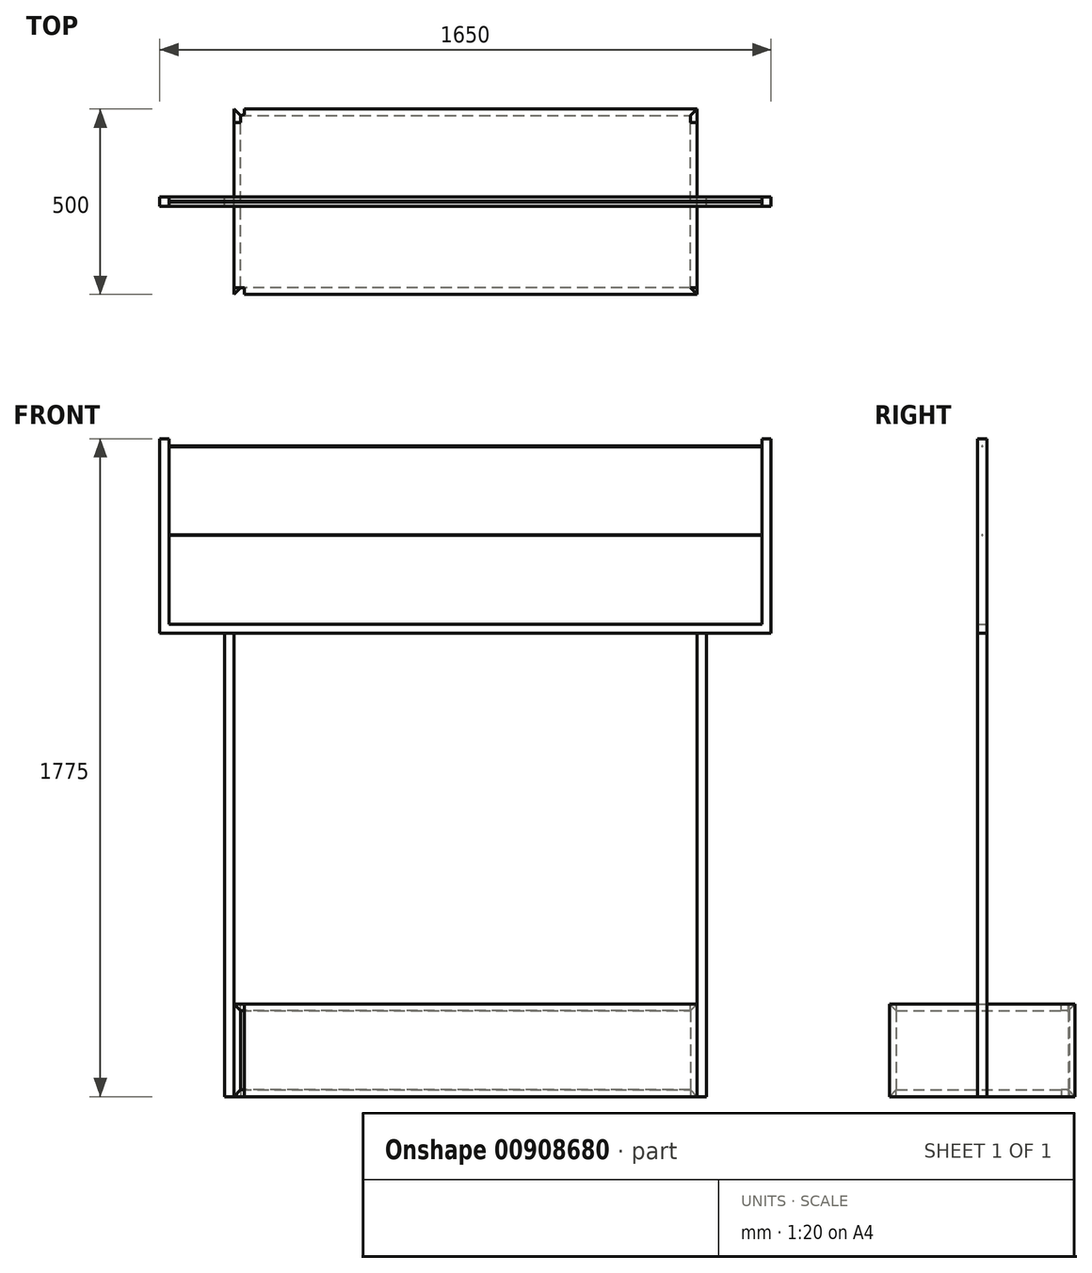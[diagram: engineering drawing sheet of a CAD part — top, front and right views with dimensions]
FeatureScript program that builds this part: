
annotation { "Feature Type Name" : "Feature", "Feature Type Description" : "" }
export const myFeature = defineFeature(function(context is Context, id is Id, definition is map)
    precondition{}
    {
        {
            var Q0;
            Q0=qCreatedBy(makeId("Front.planeOp"),FACE);
            var sketch = newSketch(context, id + "F0", { "sketchPlane" : qUnion([Q0])});
            skLineSegment(sketch, "E0", {"start": v(-625, 0) * mm, "end": v(625, 0) * mm});
            skLineSegment(sketch, "E1", {"start": v(625, 0) * mm, "end": v(607, 18) * mm});
            skLineSegment(sketch, "E2", {"start": v(607, 18) * mm, "end": v(-607, 18) * mm});
            skLineSegment(sketch, "E3", {"start": v(-607, 18) * mm, "end": v(-625, 0) * mm});
            skSolve(sketch);
        }
        {
            var Q0;
            Q0=qSketchRegion(id+"F0",true);
            extrude(context, id + "F1", {"entities" : qUnion([Q0]), "endBound" : BoundingType.SYMMETRIC, "depth" : 500 * mm, "offsetDistance" : 25 * mm});
        }
        {
            var Q0;
            Q0=qCreatedBy(makeId("Right.planeOp"),FACE);
            var sketch = newSketch(context, id + "F2", { "sketchPlane" : qUnion([Q0])});
            skLineSegment(sketch, "E4", {"start": v(-250, 0) * mm, "end": v(-231.1, 18.9) * mm});
            skLineSegment(sketch, "E5", {"start": v(-231.1, 18.9) * mm, "end": v(-231.1, 28.41) * mm});
            skLineSegment(sketch, "E6", {"start": v(-231.1, 28.41) * mm, "end": v(-266.04, 28.41) * mm});
            skLineSegment(sketch, "E7", {"start": v(-266.04, 28.41) * mm, "end": v(-266.04, 0) * mm});
            skLineSegment(sketch, "E8", {"start": v(-266.04, 0) * mm, "end": v(-250, 0) * mm});
            skLineSegment(sketch, "E9", {"start": v(250, 0) * mm, "end": v(231.1, 18.9) * mm});
            skLineSegment(sketch, "E10", {"start": v(231.1, 18.9) * mm, "end": v(231.1, 44) * mm});
            skLineSegment(sketch, "E11", {"start": v(231.1, 44) * mm, "end": v(262.92, 44) * mm});
            skLineSegment(sketch, "E12", {"start": v(262.92, 44) * mm, "end": v(262.92, 0) * mm});
            skLineSegment(sketch, "E13", {"start": v(250, 0) * mm, "end": v(262.92, 0) * mm});
            skSolve(sketch);
        }
        {
            var Q0;
            Q0=qSketchRegion(id+"F2",true);
            extrude(context, id + "F3", {"entities" : qUnion([Q0]), "operationType" : NewBodyOperationType.REMOVE, "endBound" : BoundingType.SYMMETRIC, "oppositeDirection" : true, "depth" : 1428 * mm, "offsetDistance" : 25 * mm});
        }
        {
            var Q0;
            Q0=qCreatedBy(makeId("Right.planeOp"),FACE);
            var sketch = newSketch(context, id + "F4", { "sketchPlane" : qUnion([Q0])});
            skLineSegment(sketch, "E14.0", {"start": v(232, 18) * mm, "end": v(250, 0) * mm});
            skLineSegment(sketch, "E14.1", {"start": v(-232, 18) * mm, "end": v(-250, 0) * mm});
            skLineSegment(sketch, "E15", {"start": v(232, 18) * mm, "end": v(232, 232) * mm});
            skLineSegment(sketch, "E16", {"start": v(232, 232) * mm, "end": v(250, 250) * mm});
            skLineSegment(sketch, "E17", {"start": v(250, 250) * mm, "end": v(250, 0) * mm});
            skLineSegment(sketch, "E18", {"start": v(-232, 18) * mm, "end": v(-232, 232) * mm});
            skLineSegment(sketch, "E19", {"start": v(-232, 232) * mm, "end": v(-250, 250) * mm});
            skLineSegment(sketch, "E20", {"start": v(-250, 250) * mm, "end": v(-250, 0) * mm});
            skSolve(sketch);
        }
        {
            var Q0;
            Q0=makeQuery(id+"F4.imprint","IMPRINT",FACE,{"disambiguationData":[TD([[makeQuery(id+"F4.imprint","IMPRINT",EDGE,{"derivedFrom":sQuery(id+"F4.wireOp",EDGE,"E14.0")}),1.0]])]});
            var Q1;
            Q1=makeQuery(id+"F4.imprint","IMPRINT",FACE,{"disambiguationData":[TD([[makeQuery(id+"F4.imprint","IMPRINT",EDGE,{"derivedFrom":sQuery(id+"F4.wireOp",EDGE,"E14.1")}),-1.0]])]});
            var Q2;
            Q2=makeQuery(id+"F1.opExtrude","CAP_VERTEX",VERTEX,{"disambiguationData":[OSD([sQuery(id+"F0.wireOp",EDGE,"E0"),sQuery(id+"F0.wireOp",EDGE,"E1")])],"isStart":true});
            extrude(context, id + "F5", {"entities" : qUnion([Q0, Q1]), "endBound" : BoundingType.SYMMETRIC, "depth" : 1250 * mm, "endBoundEntityVertex" : qUnion([Q2]), "offsetDistance" : 25 * mm});
        }
        {
            var Q0;
            Q0=qCreatedBy(makeId("Top.planeOp"),FACE);
            var sketch = newSketch(context, id + "F6", { "sketchPlane" : qUnion([Q0])});
            skLineSegment(sketch, "E21", {"start": v(-625, 250) * mm, "end": v(-607, 232) * mm});
            skLineSegment(sketch, "E22", {"start": v(-607, 232) * mm, "end": v(-607, 212.8) * mm});
            skLineSegment(sketch, "E23", {"start": v(-607, 212.8) * mm, "end": v(-625, 212.8) * mm});
            skLineSegment(sketch, "E24", {"start": v(-625, 212.8) * mm, "end": v(-625, 250) * mm});
            skLineSegment(sketch, "E25", {"start": v(-607, -232) * mm, "end": v(-625, -250) * mm});
            skLineSegment(sketch, "E26", {"start": v(-625, -250) * mm, "end": v(-638.85, -250) * mm});
            skLineSegment(sketch, "E27", {"start": v(-638.85, -250) * mm, "end": v(-638.85, -232) * mm});
            skLineSegment(sketch, "E28", {"start": v(-638.85, -232) * mm, "end": v(-607, -232) * mm});
            skLineSegment(sketch, "E29.MirrorCS", {"start": v(625, 250) * mm, "end": v(607, 232) * mm});
            skLineSegment(sketch, "E30.MirrorCS", {"start": v(638.85, -232) * mm, "end": v(607, -232) * mm});
            skLineSegment(sketch, "E31.MirrorCS", {"start": v(638.85, -250) * mm, "end": v(638.85, -232) * mm});
            skLineSegment(sketch, "E32.MirrorCS", {"start": v(607, -232) * mm, "end": v(625, -250) * mm});
            skLineSegment(sketch, "E33.MirrorCS", {"start": v(607, 232) * mm, "end": v(607, 212.8) * mm});
            skLineSegment(sketch, "E34.MirrorCS", {"start": v(625, -250) * mm, "end": v(638.85, -250) * mm});
            skLineSegment(sketch, "E35.MirrorCS", {"start": v(607, 212.8) * mm, "end": v(625, 212.8) * mm});
            skLineSegment(sketch, "E36.MirrorCS", {"start": v(625, 212.8) * mm, "end": v(625, 250) * mm});
            skSolve(sketch);
        }
        {
            var Q0;
            Q0=qSketchRegion(id+"F6",true);
            extrude(context, id + "F7", {"entities" : qUnion([Q0]), "operationType" : NewBodyOperationType.REMOVE, "endBound" : BoundingType.SYMMETRIC, "depth" : 1216 * mm, "offsetDistance" : 25 * mm});
        }
        {
            var Q0;
            Q0=qCreatedBy(makeId("Front.planeOp"),FACE);
            var sketch = newSketch(context, id + "F8", { "sketchPlane" : qUnion([Q0])});
            skLineSegment(sketch, "E37.0", {"start": v(-625, 0) * mm, "end": v(-607, 18) * mm});
            skLineSegment(sketch, "E37.1", {"start": v(-607, 232) * mm, "end": v(-607, 18) * mm});
            skLineSegment(sketch, "E37.2", {"start": v(-625, 250) * mm, "end": v(-625, 0) * mm});
            skLineSegment(sketch, "E37.3", {"start": v(-607, 232) * mm, "end": v(-625, 250) * mm});
            skSolve(sketch);
        }
        {
            var Q0;
            Q0=qSketchRegion(id+"F8",true);
            extrude(context, id + "F9", {"entities" : qUnion([Q0]), "endBound" : BoundingType.SYMMETRIC, "depth" : 500 * mm, "offsetDistance" : 25 * mm});
        }
        {
            var Q0;
            Q0=qCreatedBy(makeId("Top.planeOp"),FACE);
            var sketch = newSketch(context, id + "F10", { "sketchPlane" : qUnion([Q0])});
            skLineSegment(sketch, "E38.0", {"start": v(-607, -232) * mm, "end": v(-625, -250) * mm});
            skLineSegment(sketch, "E38.1", {"start": v(-607, 232) * mm, "end": v(-625, 250) * mm});
            skLineSegment(sketch, "E39", {"start": v(-625, 250) * mm, "end": v(-625, 288.49) * mm});
            skLineSegment(sketch, "E40", {"start": v(-625, 288.49) * mm, "end": v(-596.8, 288.49) * mm});
            skLineSegment(sketch, "E41", {"start": v(-596.8, 288.49) * mm, "end": v(-596.8, 234.6) * mm});
            skLineSegment(sketch, "E42", {"start": v(-596.8, 234.6) * mm, "end": v(-607, 232) * mm});
            skLineSegment(sketch, "E43", {"start": v(-607, -232) * mm, "end": v(-596.8, -232) * mm});
            skLineSegment(sketch, "E44", {"start": v(-596.8, -232) * mm, "end": v(-596.8, -280.72) * mm});
            skLineSegment(sketch, "E45", {"start": v(-596.8, -280.72) * mm, "end": v(-625, -280.72) * mm});
            skLineSegment(sketch, "E46", {"start": v(-625, -280.72) * mm, "end": v(-625, -250) * mm});
            skSolve(sketch);
        }
        {
            var Q0;
            Q0=qSketchRegion(id+"F10",true);
            extrude(context, id + "F11", {"entities" : qUnion([Q0]), "operationType" : NewBodyOperationType.REMOVE, "endBound" : BoundingType.SYMMETRIC, "depth" : 1068 * mm, "offsetDistance" : 25 * mm});
        }
        {
            var Q0;
            Q0=makeQuery(id+"F9.opExtrude","SWEPT_BODY",BODY,{"disambiguationData":[OSD([sQuery(id+"F8.wireOp",EDGE,"E37.0"),sQuery(id+"F8.wireOp",EDGE,"E37.1"),sQuery(id+"F8.wireOp",EDGE,"E37.2"),sQuery(id+"F8.wireOp",EDGE,"E37.3")])]});
            var Q1;
            Q1=qCreatedBy(makeId("Right.planeOp"),FACE);
            mirror(context, id + "F12", {"entities" : qUnion([Q0]), "mirrorPlane" : qUnion([Q1])});
        }
        {
            var Q0;
            Q0=qCreatedBy(makeId("Top.planeOp"),FACE);
            cPlane(context, id + "F13", {"entities" : qUnion([Q0]), "cplaneType" : CPlaneType.OFFSET, "offset" : 125 * mm, "width" : 150 * mm, "height" : 150 * mm});
        }
        {
            var Q0;
            Q0=makeQuery(id+"F1.opExtrude","SWEPT_BODY",BODY,{"disambiguationData":[OSD([sQuery(id+"F0.wireOp",EDGE,"E0"),sQuery(id+"F0.wireOp",EDGE,"E1"),sQuery(id+"F0.wireOp",EDGE,"E2"),sQuery(id+"F0.wireOp",EDGE,"E3")])]});
            var Q1;
            Q1=qCreatedBy(id+"F13.planeOp",FACE);
            mirror(context, id + "F14", {"entities" : qUnion([Q0]), "mirrorPlane" : qUnion([Q1])});
        }
        {
            var Q0;
            Q0=qCreatedBy(makeId("Front.planeOp"),FACE);
            var sketch = newSketch(context, id + "F15", { "sketchPlane" : qUnion([Q0])});
            skLineSegment(sketch, "E47.bottom", {"start": v(625, 0) * mm, "end": v(650, 0) * mm});
            skLineSegment(sketch, "E47.top", {"start": v(625, 1250) * mm, "end": v(650, 1250) * mm});
            skLineSegment(sketch, "E47.left", {"start": v(625, 0) * mm, "end": v(625, 1250) * mm});
            skLineSegment(sketch, "E47.right", {"start": v(650, 0) * mm, "end": v(650, 1250) * mm});
            skLineSegment(sketch, "E48.bottom", {"start": v(-625, 0) * mm, "end": v(-650, 0) * mm});
            skLineSegment(sketch, "E48.top", {"start": v(-625, 1250) * mm, "end": v(-650, 1250) * mm});
            skLineSegment(sketch, "E48.left", {"start": v(-625, 0) * mm, "end": v(-625, 1250) * mm});
            skLineSegment(sketch, "E48.right", {"start": v(-650, 0) * mm, "end": v(-650, 1250) * mm});
            skSolve(sketch);
        }
        {
            var Q0;
            Q0=qSketchRegion(id+"F15",true);
            extrude(context, id + "F16", {"entities" : qUnion([Q0]), "endBound" : BoundingType.SYMMETRIC, "depth" : 25 * mm, "offsetDistance" : 25 * mm});
        }
        {
            var Q0;
            Q0=qCreatedBy(makeId("Front.planeOp"),FACE);
            var sketch = newSketch(context, id + "F17", { "sketchPlane" : qUnion([Q0])});
            skLineSegment(sketch, "E49.bottom", {"start": v(-825, 1250) * mm, "end": v(825, 1250) * mm});
            skLineSegment(sketch, "E49.top", {"start": v(-800, 1275) * mm, "end": v(800, 1275) * mm});
            skLineSegment(sketch, "E49.left", {"start": v(-825, 1250) * mm, "end": v(-825, 1275) * mm});
            skLineSegment(sketch, "E49.right", {"start": v(825, 1250) * mm, "end": v(825, 1275) * mm});
            skPoint(sketch, "E50", {"position": v(0, 1250) * mm});
            skLineSegment(sketch, "E51", {"start": v(-825, 1775) * mm, "end": v(-825, 1275) * mm});
            skLineSegment(sketch, "E52", {"start": v(-825, 1775) * mm, "end": v(-800, 1775) * mm});
            skLineSegment(sketch, "E53", {"start": v(-800, 1775) * mm, "end": v(-800, 1275) * mm});
            skLineSegment(sketch, "E54", {"start": v(825, 1275) * mm, "end": v(825, 1775) * mm});
            skLineSegment(sketch, "E55", {"start": v(825, 1775) * mm, "end": v(800, 1775) * mm});
            skLineSegment(sketch, "E56", {"start": v(800, 1775) * mm, "end": v(800, 1275) * mm});
            skSolve(sketch);
        }
        {
            var Q0;
            Q0=qSketchRegion(id+"F17",true);
            extrude(context, id + "F18", {"entities" : qUnion([Q0]), "endBound" : BoundingType.SYMMETRIC, "depth" : 25 * mm, "offsetDistance" : 25 * mm});
        }
        {
            var Q0;
            Q0=makeQuery(id+"F18.opExtrude","SWEPT_FACE",FACE,{"disambiguationData":[OSD([sQuery(id+"F17.wireOp",EDGE,"E53")])]});
            var sketch = newSketch(context, id + "F19", { "sketchPlane" : qUnion([Q0])});
            skCircle(sketch, "E57", {"center": v(0, 1755) * mm, "radius": 1 * mm});
            skSolve(sketch);
        }
        {
            var Q0;
            Q0 = qSketchRegion(id + "F19", true);
            var Q1;
            Q1=makeQuery(id+"F18.opExtrude","CAP_VERTEX",VERTEX,{"disambiguationData":[OSD([sQuery(id+"F17.wireOp",EDGE,"E55"),sQuery(id+"F17.wireOp",EDGE,"E56")])],"isStart":false});
            extrude(context, id + "F20", {"entities" : qUnion([Q0]), "endBound" : BoundingType.UP_TO_VERTEX, "depth" : 25 * mm, "endBoundEntityVertex" : qUnion([Q1]), "offsetDistance" : 25 * mm});
        }
        {
            var Q0;
            Q0=makeQuery(id+"F20.opExtrude","SWEPT_BODY",BODY,{"disambiguationData":[OSD([sQuery(id+"F19.wireOp",EDGE,"E57")])]});
            var Q1;
            Q1=makeQuery(id+"F18.opExtrude","CAP_EDGE",EDGE,{"disambiguationData":[OSD([sQuery(id+"F17.wireOp",EDGE,"E53")])],"isStart":false});
            transform(context, id + "F21", {"entities" : qUnion([Q0]), "transformType" : TransformType.TRANSLATION_3D, "dx" : 0 * mm, "dy" : 0 * mm, "dz" : -240 * mm, "makeCopy" : true});
        }
    });
